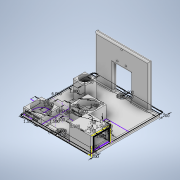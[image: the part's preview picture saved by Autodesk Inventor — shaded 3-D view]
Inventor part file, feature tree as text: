
AUTODESK INVENTOR PART (.ipt)
format: ipt  version: 2020 (Build 240168000, 168)  size: 1,740,800 bytes
history: native  units: in
note: dims shown in document units (in); Inventor stores cm internally (conversion verified against a paired STEP export)
features: extrude x15, sketch x9, fillet x7, hole x2
ambient origin geometry x8: Origin, YZ Plane, XZ Plane, XY Plane, X Axis, Y Axis, Z Axis, Center Point
bodies: Solid1 (feature_tree)
feature tree (33):
  sketch  "Sketch1"  dims[d0=5.6in d1=6.0in]
  extrude  "Extrusion1"  Depth=6.0in
  hole  "Hole1"  [1 undecoded]
  extrude  "Extrusion2"  Depth=5.6in
  extrude  "Extrusion3"  Depth=5.6in
  extrude  "Extrusion4"  Depth=0.25in TaperAngle=0.0deg
  extrude  "Extrusion5"  Depth=1.5in
  extrude  "Extrusion6"  Depth=1.5in
  hole  "Hole2"  [1 undecoded]
  extrude  "Extrusion7"  TaperAngle=180.0deg  [1 undecoded]
  extrude  "Extrusion8"  Depth=1.5in
  extrude  "Extrusion9"  Depth=1.5in
  sketch  "Sketch6"  dims[d11=0.266in d12=0.75in d13=0.625in d14=0.19in d15=0.5635in d16=1.0in d17=0.8108in d18=1.5in]
  extrude  "Extrusion10"  Depth=1.5in
  sketch  "Sketch7"  dims[d19=0.6in d20=1.5in]
  extrude  "Extrusion11"  Depth=1.5in
  extrude  "Extrusion12"  Depth=1.3in
  extrude  "Extrusion13"  Depth=1.3in
  fillet  "Fillet1"  Radius=0.5in
  fillet  "Fillet2"  Radius=0.5in
  fillet  "Fillet3"  Radius=1.0in
  fillet  "Fillet4"  Radius=1.5in
  fillet  "Fillet5"  Radius=0.325in
  fillet  "Fillet6"  Radius=2.0in
  fillet  "Fillet7"  Radius=1.5in
  sketch  "Sketch8"  dims[d21=1.5in d22=0.6in]
  sketch  "Sketch9"  dims[d23=1.5in d24=180.0deg d25=1.5in d26=1.5in d27=1.5in d28=1.5in d29=1.3in d30=1.3in d31=0.5in d32=0.0in d33=0.5in d34=0.0in d35=1.0in d36=0.0in d37=1.5in d38=0.325in d39=2.0in d40=0.0in d41=1.5in d42=0.0in d43=0.333in d44=0.96in d45=0.356in d46=0.356in d47=0.134in d48=0.75in d49=0.256in d50=0.118in d51=90.0deg d52=1.0in d53=0.8108in d54=1.75in d55=1.0in d56=1.0in d57=1.0in d58=0.78in d59=1.5in d60=0.0in d61=0.25in d62=0.25in d63=1.5in d64=0.0in d65=1.25in d66=0.0in d67=0.125in d68=0.125in d69=0.125in d70=0.125in d71=1.725in d72=0.0in d73=0.25in d74=0.25in d75=1.043in d76=0.748in d77=0.25in d78=0.0in d79=0.25in d80=0.25in d81=0.0625in d82=0.0625in d83=0.0625in d84=0.0625in d85=0.1875in d86=0.0in d87=0.125in d88=0.0in d89=0.125in d90=0.125in d91=0.0625in d92=0.0625in d93=0.0625in d94=0.0625in d95=0.0625in d96=0.0197in d97=0.0in d98=0.0197in d99=0.0in]
  extrude  "Extrusion14"  Depth=0.333in
  extrude  "Extrusion15"  Depth=0.96in
  sketch  "Sketch2"  dims[d2=0.5in d3=90.0deg]
  sketch  "Sketch3"  dims[d4=0.5in d5=5.6in]
  sketch  "Sketch4"  dims[d6=0.2in d7=5.6in]
  sketch  "Sketch5"  dims[d8=0.2in d9=0.25in d10=0.0in]
note: 3 required parameter values undecoded (feature->parameter linkage not recoverable at this tier; creation-order binding heuristic only, values carry confidence <= 0.55)
